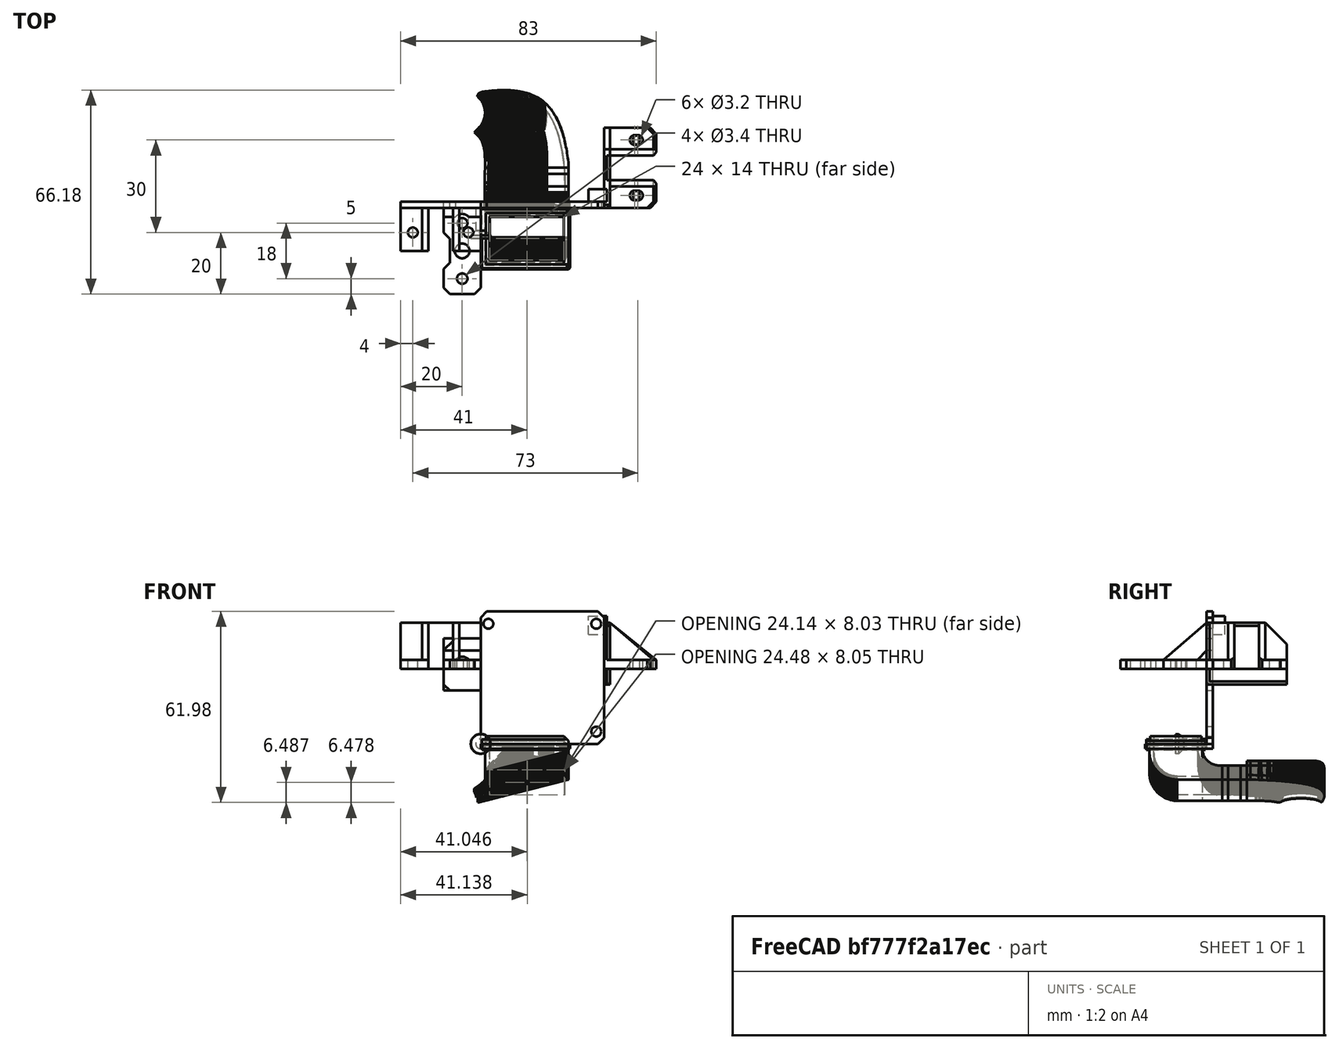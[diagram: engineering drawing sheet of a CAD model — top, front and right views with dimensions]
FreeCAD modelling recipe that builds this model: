
FCSTD DOCUMENT  (FreeCAD 0.18R14555 (Git shallow))
Label: hemera-duct-4020
License: All rights reserved
LicenseURL: http://en.wikipedia.org/wiki/All_rights_reserved
objects: Part::Box×24, Part::Chamfer×19, Part::Feature×14, Part::Cut×12, Part::Cylinder×9, Part::MultiFuse×7, Part::MultiCommon×4
note: 89 computed .brp shape members not serialized (recipe doc carries the construction recipe); baked Part::Feature solids carry a one-line shape summary decoded from their .brp

FEATURE [Part::Feature] ductv5final001001_solid  label="original-duct"
  Placement = pos=(28.59,113.29,116.01) rot=(0.707107,0,-0.707107;3.14159rad)
  shape: bbox 30.66 x 55.77 x 19.97 mm, 22506 faces (baked)
FEATURE [Part::Box] Box001  label="Cube001"
  AttacherType = Attacher::AttachEngine3D
  Height = 38
  Length = 40
  Placement = pos=(-3,11,-20) rot=(0,0,1;0rad)
  Width = 26
FEATURE [Part::Box] Box002  label="Cube002"
  AttacherType = Attacher::AttachEngine3D
  Height = 38
  Length = 40
  Placement = pos=(-3,-21,-20) rot=(0,0,1;0rad)
  Width = 26
FEATURE [Part::Box] Box003  label="Cube003"
  AttacherType = Attacher::AttachEngine3D
  Height = 38
  Length = 40
  Placement = pos=(-3,5,-20) rot=(0,0,1;0rad)
  Width = 6
FEATURE [Part::Feature] ductv5final001001_solid001  label="original-duct001"
  Placement = pos=(28.59,113.29,116.01) rot=(0.707107,0,-0.707107;3.14159rad)
  shape: bbox 30.66 x 55.77 x 19.97 mm, 22506 faces (baked)
FEATURE [Part::Feature] ductv5final001001_solid002  label="original-duct002"
  Placement = pos=(28.59,113.29,116.01) rot=(0.707107,0,-0.707107;3.14159rad)
  shape: bbox 30.66 x 55.77 x 19.97 mm, 22506 faces (baked)
FEATURE [Part::MultiCommon] Common  label="duct-tail"
  Placement = pos=(0,2,1.5) rot=(0,0,1;0rad)
  Shapes = -> [ductv5final001001_solid,Box001]
FEATURE [Part::MultiCommon] Common001  label="duct-head"
  Shapes = -> [ductv5final001001_solid001,Box002]
FEATURE [Part::MultiCommon] Common002  label="duct-mid-1"
  Shapes = -> [ductv5final001001_solid002,Box003]
FEATURE [Part::Feature] Common002001  label="duct-mid-2"
  Placement = pos=(0,2,0) rot=(0,0,1;0rad)
  shape: bbox 27.18 x 6 x 11.5 mm, 1454 faces (baked)
FEATURE [Part::Box] Box004  label="Cube004"
  AttacherType = Attacher::AttachEngine3D
  Height = 1.5
  Length = 29
  Placement = pos=(0,-20,-2) rot=(0,0,1;0rad)
  Width = 22
FEATURE [Part::Box] Box005  label="Cube005"
  AttacherType = Attacher::AttachEngine3D
  Height = 1.5
  Length = 24
  Placement = pos=(3,-17,-2) rot=(0,0,1;0rad)
  Width = 14
FEATURE [Part::Cylinder] Cylinder
  Angle = 360
  AttacherType = Attacher::AttachEngine3D
  Height = 10
  Placement = pos=(0,0,0) rot=(1,0,0;1.5708rad)
  Radius = 1.6
FEATURE [Part::Cylinder] Cylinder001
  Angle = 360
  AttacherType = Attacher::AttachEngine3D
  Height = 3
  Placement = pos=(0,0,0) rot=(1,0,0;1.5708rad)
  Radius = 3.2
FEATURE [Part::Chamfer] Chamfer
  Base = -> Cylinder001
  Edges = 1 edges r=2: [Edge3]
  Placement = pos=(0,-7,0) rot=(0,0,1;0rad)
FEATURE [Part::MultiFuse] Fusion  label="screw-template"
  Shapes = -> [Chamfer,Cylinder]
FEATURE [Part::Box] Box009  label="Cube009"
  AttacherType = Attacher::AttachEngine3D
  Height = 6
  Length = 6
  Placement = pos=(35,2,35.5) rot=(0,0,1;0rad)
  Width = 4
FEATURE [Part::Feature] Cut002003004006002  label="Cut002003004008"
  Placement = pos=(0,2,0) rot=(0,0,-1;1.5708rad)
  shape: bbox 15 x 26 x 43 mm, 23 faces (baked)
FEATURE [Part::Chamfer] Chamfer007
  Base = -> Cut002003004006002
  Edges = 1 edges r=1: [Edge8]
FEATURE [Part::Box] Box013  label="Cube013"
  AttacherType = Attacher::AttachEngine3D
  Height = 11
  Length = 10
  Placement = pos=(43,15.5,27.3) rot=(0,0,1;0rad)
  Width = 10
FEATURE [Part::Cut] Cut002003004006003
  Base = -> Chamfer007
  Tool = -> Box013
FEATURE [Part::Box] Box014  label="Cube014"
  AttacherType = Attacher::AttachEngine3D
  Height = 11
  Length = 2
  Placement = pos=(43,12,23.3) rot=(0,0,1;0rad)
  Width = 11
FEATURE [Part::Cut] Cut002003004006004
  Base = -> Cut002003004006003
  Placement = pos=(-1,30,0) rot=(0,0,1;0rad)
  Tool = -> Box014
FEATURE [Part::Box] Box015  label="Cube015"
  AttacherType = Attacher::AttachEngine3D
  Height = 3
  Length = 12
  Placement = pos=(40,0,24.3) rot=(0,0,1;0rad)
  Width = 26
FEATURE [Part::Box] Box016  label="Cube016"
  AttacherType = Attacher::AttachEngine3D
  Height = 18.7
  Length = 2
  Placement = pos=(40,0,24.3) rot=(0,0,1;0rad)
  Width = 26
FEATURE [Part::Box] Box017  label="Cube017"
  AttacherType = Attacher::AttachEngine3D
  Height = 3
  Length = 7
  Placement = pos=(46,32,24.3) rot=(0,0,1;0rad)
  Width = 26
FEATURE [Part::Cut] Cut002003004006006
  Base = -> Box017
  Placement = pos=(-3,-32,0) rot=(0,0,1;0rad)
  Tool = -> Cut002003004006004
FEATURE [Part::Cut] Cut002003004006007
  Base = -> Box015
  Tool = -> Cut002003004006006
FEATURE [Part::Feature] Body003
  Placement = pos=(-14,9,17) rot=(0,0,1;0rad)
  shape: bbox 10 x 2 x 16 mm, 5 faces (baked)
FEATURE [Part::Feature] Body004
  Placement = pos=(-14,19,17) rot=(0,0,1;0rad)
  shape: bbox 10 x 2 x 16 mm, 5 faces (baked)
FEATURE [Part::MultiFuse] Fusion011
  Placement = pos=(-26,42,0) rot=(0,0,-1;1.5708rad)
  Shapes = -> [Body004,Body003,Cut002003004006007,Box016]
FEATURE [Part::Box] Box018  label="Cube018"
  AttacherType = Attacher::AttachEngine3D
  Height = 16
  Length = 26
  Placement = pos=(-26,-14,27.3) rot=(0,0,1;0rad)
  Width = 23
FEATURE [Part::Cut] Cut002003004006008
  Base = -> Fusion011
  Placement = pos=(0,-4,0) rot=(0,0,1;0rad)
  Tool = -> Box018
FEATURE [Part::Box] Box019  label="Cube019"
  AttacherType = Attacher::AttachEngine3D
  Height = 12
  Length = 26
  Placement = pos=(-26,0,27.3) rot=(0,0,1;0rad)
  Width = 2
FEATURE [Part::Box] Box020  label="Cube020"
  AttacherType = Attacher::AttachEngine3D
  Height = 10
  Length = 8
  Placement = pos=(-17,-14,23) rot=(0,0,1;0rad)
  Width = 14
FEATURE [Part::Cut] Cut
  Base = -> Box004
  Placement = pos=(0,0,0.5) rot=(0,0,1;0rad)
  Tool = -> Box005
FEATURE [Part::Box] Box  label="Cube"
  AttacherType = Attacher::AttachEngine3D
  Height = 43
  Length = 40
  Width = 2
FEATURE [Part::Cylinder] Cylinder003
  Angle = 360
  AttacherType = Attacher::AttachEngine3D
  Height = 10
  Placement = pos=(37.5,2,4) rot=(1,0,0;1.5708rad)
  Radius = 1.6
FEATURE [Part::Cylinder] Cylinder004
  Angle = 360
  AttacherType = Attacher::AttachEngine3D
  Height = 10
  Placement = pos=(2.5,2,39) rot=(1,0,0;1.5708rad)
  Radius = 1.6
FEATURE [Part::Cylinder] Cylinder005
  Angle = 360
  AttacherType = Attacher::AttachEngine3D
  Height = 10
  Placement = pos=(37.5,2,39) rot=(1,0,0;1.5708rad)
  Radius = 1.6
FEATURE [Part::Box] Box021  label="Cube021"
  AttacherType = Attacher::AttachEngine3D
  Height = 10
  Length = 9
  Placement = pos=(-10,21,-20) rot=(0,0,1;0rad)
  Width = 21
FEATURE [Part::Chamfer] Chamfer010
  Base = -> Cut
  Edges = 2 edges r=0.5: [Edge1,Edge6]
FEATURE [Part::MultiFuse] Fusion012
  Shapes = -> [Cylinder004,Cylinder005,Cylinder003]
FEATURE [Part::Cut] Cut002003004006010
  Base = -> Box
  Tool = -> Fusion012
FEATURE [Part::Chamfer] Chamfer011
  Base = -> Cut002003004006010
  Edges = 3 edges r=2: [Edge2,Edge12,Edge18]
FEATURE [Part::Box] Box022  label="Cube022"
  AttacherType = Attacher::AttachEngine3D
  Height = 3
  Length = 26
  Placement = pos=(-26,-3,24.3) rot=(0,0,1;0rad)
  Width = 5
FEATURE [Part::Feature] Fusion014001  label="Fusion015"
  Placement = pos=(42,26,0) rot=(0,0,1;1.5708rad)
  shape: bbox 17 x 26 x 15 mm, 20 faces (baked)
FEATURE [Part::Feature] Common002002  label="duct-tail001"
  Placement = pos=(0,2,1.5) rot=(0,0,1;0rad)
  shape: bbox 30.57 x 25.18 x 12 mm, 11674 faces (baked)
FEATURE [Part::Chamfer] Chamfer012
  Base = -> Fusion014001
  Edges = 2 edges r=2: [Edge6,Edge31]
FEATURE [Part::Chamfer] Chamfer013
  Base = -> Chamfer012
  Edges = 4 edges r=1: [Edge5,Edge6,Edge42,Edge43]
FEATURE [Part::Chamfer] Chamfer014
  Base = -> Chamfer013
  Edges = 1 edges r=7: [Edge37]
FEATURE [Part::Cut] Cut002003004006012
  Base = -> Common002002
  Placement = pos=(0,0,-1.5) rot=(0,0,1;0rad)
  Tool = -> Box021
FEATURE [Part::Chamfer] Chamfer015
  Base = -> Chamfer014
  Edges = 1 edges r=1: [Edge3]
FEATURE [Part::Box] Box023  label="Cube023"
  AttacherType = Attacher::AttachEngine3D
  Height = 5
  Length = 2
  Placement = pos=(40,0,19.3) rot=(0,0,1;0rad)
  Width = 26
FEATURE [Part::MultiFuse] Fusion014002
  Shapes = -> [Chamfer015,Box023]
FEATURE [Part::Feature] Body005
  Placement = pos=(-9,28,1.3) rot=(0,0,1;0rad)
  shape: bbox 2 x 14 x 12 mm, 5 faces (baked)
FEATURE [Part::Feature] Body006
  Placement = pos=(-19,28,1.3) rot=(0,0,1;0rad)
  shape: bbox 2 x 14 x 12 mm, 5 faces (baked)
FEATURE [Part::MultiFuse] Fusion014003
  Shapes = -> [Body006,Body005,Cut002003004006008,Box022,Box019]
FEATURE [Part::Cut] Cut002003004006013
  Base = -> Fusion014003
  Tool = -> Box020
FEATURE [Part::Feature] Cut002003004006013001  label="Cut002003004006014"
  Placement = pos=(42,26,0) rot=(0,0,1;1.5708rad)
  shape: bbox 16 x 26 x 15 mm, 20 faces (baked)
FEATURE [Part::Box] Box024  label="Cube024"
  AttacherType = Attacher::AttachEngine3D
  Height = 5
  Length = 2
  Placement = pos=(40,0,19.3) rot=(0,0,1;0rad)
  Width = 26
FEATURE [Part::Chamfer] Chamfer016
  Base = -> Cut002003004006013001
  Edges = 2 edges r=2: [Edge16,Edge31]
FEATURE [Part::Chamfer] Chamfer017
  Base = -> Chamfer016
  Edges = 4 edges r=0.5: [Edge5,Edge6,Edge43,Edge44]
FEATURE [Part::Chamfer] Chamfer018
  Base = -> Chamfer017
  Edges = 1 edges r=7: [Edge38]
FEATURE [Part::Chamfer] Chamfer019
  Base = -> Chamfer018
  Edges = 1 edges r=1: [Edge6]
FEATURE [Part::Chamfer] Chamfer020
  Base = -> Chamfer019
  Edges = 1 edges r=1: [Edge23]
FEATURE [Part::Chamfer] Chamfer021
  Base = -> Box024
  Edges = 2 edges r=1: [Edge5,Edge8]
FEATURE [Part::Box] Box025  label="Cube025"
  AttacherType = Attacher::AttachEngine3D
  Height = 10
  Length = 12
  Placement = pos=(-12,0,24.3) rot=(0,0,1;0rad)
  Width = 2
FEATURE [Part::Box] Box026  label="Cube026"
  AttacherType = Attacher::AttachEngine3D
  Height = 3
  Length = 12
  Placement = pos=(-12,-28,24.3) rot=(0,0,1;0rad)
  Width = 28
FEATURE [Part::Box] Box027  label="Cube027"
  AttacherType = Attacher::AttachEngine3D
  Height = 10
  Length = 12
  Placement = pos=(-12,0,17.3) rot=(0,0,1;0rad)
  Width = 2
FEATURE [Part::Cylinder] Cylinder006
  Angle = 360
  AttacherType = Attacher::AttachEngine3D
  Height = 10
  Placement = pos=(-6,-14,20) rot=(0,0,1;0rad)
  Radius = 2.4
FEATURE [Part::Cylinder] Cylinder007
  Angle = 360
  AttacherType = Attacher::AttachEngine3D
  Height = 10
  Placement = pos=(-6,-5,20) rot=(0,0,1;0rad)
  Radius = 1.7
FEATURE [Part::Cylinder] Cylinder008
  Angle = 360
  AttacherType = Attacher::AttachEngine3D
  Height = 10
  Placement = pos=(-6,-23,20) rot=(0,0,1;0rad)
  Radius = 1.7
FEATURE [Part::MultiFuse] Fusion014004
  Shapes = -> [Cylinder006,Cylinder007,Cylinder008]
FEATURE [Part::Cut] Cut002003004006013002
  Base = -> Box026
  Tool = -> Fusion014004
FEATURE [Part::MultiFuse] Fusion014005
  Shapes = -> [Cut002003004006013002,Box027,Box025]
FEATURE [Part::Box] Box028  label="Cube028"
  AttacherType = Attacher::AttachEngine3D
  Height = 3
  Length = 2
  Placement = pos=(-12,-18,24.3) rot=(0,0,1;0rad)
  Width = 8
FEATURE [Part::Cut] Cut002003004006013003
  Base = -> Fusion014005
  Tool = -> Box028
FEATURE [Part::Chamfer] Chamfer022
  Base = -> Cut002003004006013003
  Edges = 2 edges r=1.9: [Edge27,Edge36]
FEATURE [Part::Chamfer] Chamfer023
  Base = -> Chamfer022
  Edges = 2 edges r=2: [Edge16,Edge19]
FEATURE [Part::Feature] Chamfer023001  label="Chamfer024"
  shape: bbox 12 x 30 x 17 mm, 21 faces (baked)
FEATURE [Part::Chamfer] Chamfer023002
  Base = -> Chamfer023001
  Edges = 1 edges r=3: [Edge45]
FEATURE [Part::Chamfer] Chamfer023003
  Base = -> Chamfer023002
  Edges = 1 edges r=3.9: [Edge31]
FEATURE [Part::Chamfer] Chamfer023004
  Base = -> Chamfer023003
  Edges = 1 edges r=2: [Edge6]
FEATURE [Part::Cylinder] Cylinder009
  Angle = 360
  AttacherType = Attacher::AttachEngine3D
  Height = 10
  Placement = pos=(-6,-5,27.3) rot=(0,0,1;0rad)
  Radius = 3
FEATURE [Part::Cut] Cut002003004006013004
  Base = -> Chamfer023004
  Tool = -> Cylinder009
FEATURE [Part::Feature] Common001001  label="duct-head001"
  shape: bbox 28.19 x 24.6 x 19.47 mm, 9819 faces (baked)
FEATURE [Part::Box] Box029  label="Cube029"
  AttacherType = Attacher::AttachEngine3D
  Height = 10
  Length = 38
  Placement = pos=(-1.5,-21,-3) rot=(0,0,1;0rad)
  Width = 24
FEATURE [Part::MultiCommon] Common002003
  Placement = pos=(0,0,1.5) rot=(0,0,1;0rad)
  Shapes = -> [Box029,Common001001]
